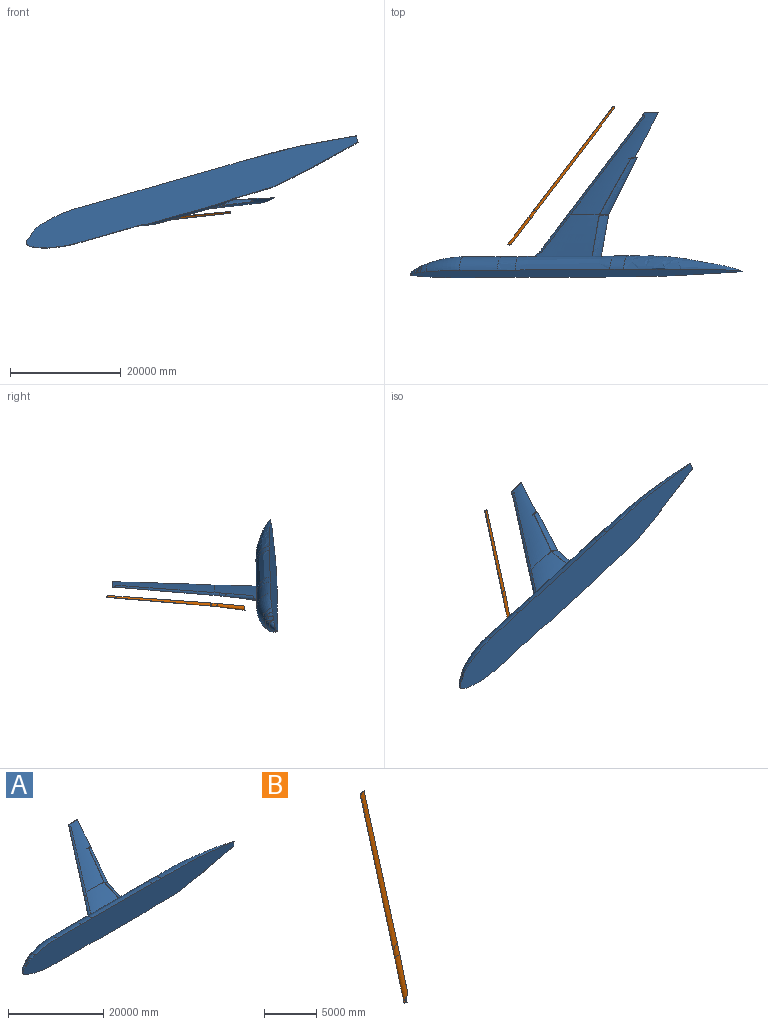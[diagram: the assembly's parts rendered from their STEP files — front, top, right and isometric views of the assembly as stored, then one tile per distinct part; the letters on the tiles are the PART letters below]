
ASSEMBLY  parts=2 mates=1
PART A: 56 faces, bbox 63756.7x30568.8x7449.2 mm
  f0: plane 572.09x512.81mm, normal (-0.02,0.98,0.22), area 43636.9mm2, adj f1,f2,f50
  f1: bspline ~7782.27x1586.75mm, area 40609.6mm2, adj f0,f2,f3
  f2: bspline ~8348.85x2997.18mm, area 30455228mm2, adj f0,f1,f3,f5,f48,f49,f51
  f3: plane 898.01x811.2mm, normal (0.05,-0.98,-0.2), area 161132.7mm2, adj f1,f2,f47
  f4: bspline ~14496x2938.62mm, area 41179474.8mm2, adj f5,f21,f22,f23,f25,f26,f27,f28
  f5: extruded ~451.44x244.18mm, area 20026.9mm2, adj f2,f4,f48,f49
  f6: bspline ~1037.93x956.47mm, area 699604.8mm2, adj f7,f12,f13,f14
  f7: bspline ~868.44x822.76mm, area 671691.1mm2, adj f6,f9,f11,f12,f14
  f8: bspline ~2088.03x1093.52mm, area 2495686.7mm2, adj f9,f14,f19
  f9: bspline ~2575.97x1701.8mm, area 4949248.2mm2, adj f7,f8,f11,f14,f19
  f10: bspline ~6488.93x6197.98mm, area 57373659.7mm2, adj f11,f15,f19
  f11: bspline ~4575.91x2066.88mm, area 7748301.6mm2, adj f7,f9,f10,f12,f19
  f12: bspline ~1164.59x987.8mm, area 860576.2mm2, adj f6,f7,f11,f13,f19
  f13: cylinder r=76.26mm len=505.32mm, axis (0.71,0,0.71), area 22982.9mm2, adj f6,f12,f14,f19
  f14: bspline ~1501.97x1352.39mm, area 770478.2mm2, adj f6,f7,f8,f9,f13,f19
  f15: cylinder r=3098.8mm len=7215.66mm, axis (1,0,0), area 70245603.1mm2, adj f10,f16,f19,f20
  f16: extruded ~4088.61x3304.2mm, area 19417129.2mm2, adj f15,f19,f20,f21
  f17: bspline ~4686.48x3164.52mm, area 16754244.9mm2, adj f18,f19,f21,f24
  f18: bspline ~22071.79x6197.79mm, area 151004088.9mm2, adj f17,f19,f24
  f19: plane 63756.7x7413.37mm, normal (0,-1,0), area 334821241.3mm2, adj f8,f9,f10,f11,f12,f13,f14,f15
  f20: bspline ~3590.54x2953.3mm, area 9796733.2mm2, adj f15,f16,f19,f22,f25
  f21: bspline ~18039.46x4771.5mm, area 98399482.6mm2, adj f4,f16,f17,f19,f22,f23
  f22: bspline ~3259.19x2665.04mm, area 8062185.9mm2, adj f4,f20,f21,f25
  f23: bspline ~3453.56x2102.63mm, area 5859172.7mm2, adj f4,f21,f24,f26
  f24: bspline ~2691.72x2677.6mm, area 6298705.6mm2, adj f17,f18,f19,f23,f25,f26
  f25: bspline ~18841.71x1604.84mm, area 26056331.4mm2, adj f4,f19,f20,f22,f24,f26
  f26: bspline ~3199.17x2038.63mm, area 3805955.1mm2, adj f4,f23,f24,f25
  f27: bspline ~13132.05x7980.6mm, area 62137076.4mm2, adj f4,f30,f31,f35,f36,f37,f38,f46
  f28: bspline ~7910.17x1559.19mm, area 20340.7mm2, adj f4,f29,f31,f41
  f29: bspline ~8321.41x2292.9mm, area 8898081.7mm2, adj f4,f28,f30,f45
  f30: bspline ~7963.94x1537.71mm, area 40726.1mm2, adj f4,f27,f29,f43
  f31: bspline ~12920.96x8015.74mm, area 61858716.1mm2, adj f4,f27,f28,f34,f36,f37,f38,f46
  f32: plane 8136.77x4203.99mm, normal (0.89,-0.46,-0.04), area 52589.3mm2, adj f33,f34,f35,f42
  f33: bspline ~2728.58x292.48mm, area 583677.9mm2, adj f32,f34,f35
  f34: bspline ~18529.33x16822.59mm, area 73360589.6mm2, adj f31,f32,f33,f35,f38,f39,f40,f41
  f35: bspline ~18551.47x16822.59mm, area 70929363.1mm2, adj f27,f32,f33,f34,f38,f39,f42,f43
  f36: plane 861.26x634.5mm, normal (0,1,0.09), area 123298.3mm2, adj f27,f31,f37
  f37: bspline ~5417.5x4267.57mm, area 5026086.4mm2, adj f27,f31,f36,f46
  f38: bspline ~19457.23x14819.13mm, area 14291061.9mm2, adj f27,f31,f34,f35,f39,f46
  f39: plane 425.72x336.22mm, normal (-0.6,-0.79,-0.07), area 25707.7mm2, adj f34,f35,f38
  f40: bspline ~10275.2x5900.04mm, area 29415.5mm2, adj f34,f41,f42,f44
  f41: bspline ~22.94x21.76mm, area 79.5mm2, adj f28,f34,f40,f45
  f42: plane 1293.4x205.8mm, normal (0.13,-0.99,-0.09), area 121695.7mm2, adj f32,f34,f35,f40,f43,f44
  f43: bspline ~10277.18x5660.13mm, area 59617.8mm2, adj f30,f35,f42,f44,f45
  f44: bspline ~10437.61x6573.08mm, area 9451707.8mm2, adj f40,f42,f43,f45
  f45: bspline ~863.94x327.48mm, area 97277.5mm2, adj f29,f41,f43,f44
  f46: bspline ~1433.09x1398.02mm, area 1064703mm2, adj f27,f31,f37,f38
  f47: plane 271.66x190.16mm, normal (0.83,-0.05,-0.56), area 32992.1mm2, adj f3,f4,f48,f49
  f48: extruded ~304.04x238.03mm, area 20836.4mm2, adj f2,f4,f5,f47
  f49: extruded ~580.74x365.78mm, area 53881.4mm2, adj f2,f4,f5,f47
  f50: bspline ~109.79x99.29mm, area 5725mm2, adj f0,f51,f52
  f51: bspline ~1045.62x636.61mm, area 104934.2mm2, adj f2,f50,f54
  f52: plane 569.43x485.67mm, normal (0,-0.96,-0.29), area 41952.3mm2, adj f50,f53,f54
  f53: bspline ~10331.65x5284.97mm, area 59202.1mm2, adj f52,f54,f55
  f54: bspline ~10904.64x6936.31mm, area 32546768.1mm2, adj f51,f52,f53,f55
  f55: plane 1100.73x630.27mm, normal (-0.03,0.88,0.48), area 107797.7mm2, adj f53,f54
PART B: 14 faces, bbox 19755.2x25808.1x2967.1 mm
  f0: bspline ~5694.7x4387.53mm, area 5049188.5mm2, adj f1,f2,f3,f5
  f1: bspline ~4735.5x3643.83mm, area 15231.7mm2, adj f0,f3,f4,f6
  f2: bspline ~5041.4x3761.4mm, area 16067.6mm2, adj f0,f3,f4,f7
  f3: plane 802.22x625.12mm, normal (-0.07,-0.98,0.2), area 111863.3mm2, adj f0,f1,f2,f4
  f4: bspline ~6035.3x4709.65mm, area 6838554mm2, adj f1,f2,f3,f8
  f5: bspline ~1344.7x1238.81mm, area 1062074.1mm2, adj f0,f6,f7,f9
  f6: bspline ~1345.26x1026.27mm, area 4494.2mm2, adj f1,f5,f8,f10
  f7: bspline ~1081.43x815.74mm, area 3136.5mm2, adj f2,f5,f8,f11
  f8: bspline ~1376.15x1344.73mm, area 1415574.5mm2, adj f4,f6,f7,f13
  f9: bspline ~19505.38x14868.94mm, area 14464025.5mm2, adj f5,f10,f11,f12
  f10: bspline ~18622.55x14112.07mm, area 59635mm2, adj f6,f9,f12,f13
  f11: bspline ~18866.55x14304.84mm, area 60270.4mm2, adj f7,f9,f12,f13
  f12: plane 383.87x298.22mm, normal (0.6,0.79,0.07), area 22966.3mm2, adj f9,f10,f11,f13
  f13: bspline ~19785.01x15157.61mm, area 21250200.6mm2, adj f8,f10,f11,f12
PLACE A rot(axis=(-0.6,-0.79,-0.07),20deg) t=(2001.98,-993.24,-6071.55)mm
PLACE B rot(axis=(0.55,0.83,0.06),4.8deg) t=(-5358.88,1330.85,283.2)mm
MATE parallel B.f12 <-> A.f39  axis (0.6,0.79,0.07) through (39752.36,30480.78,4859.69)mm
